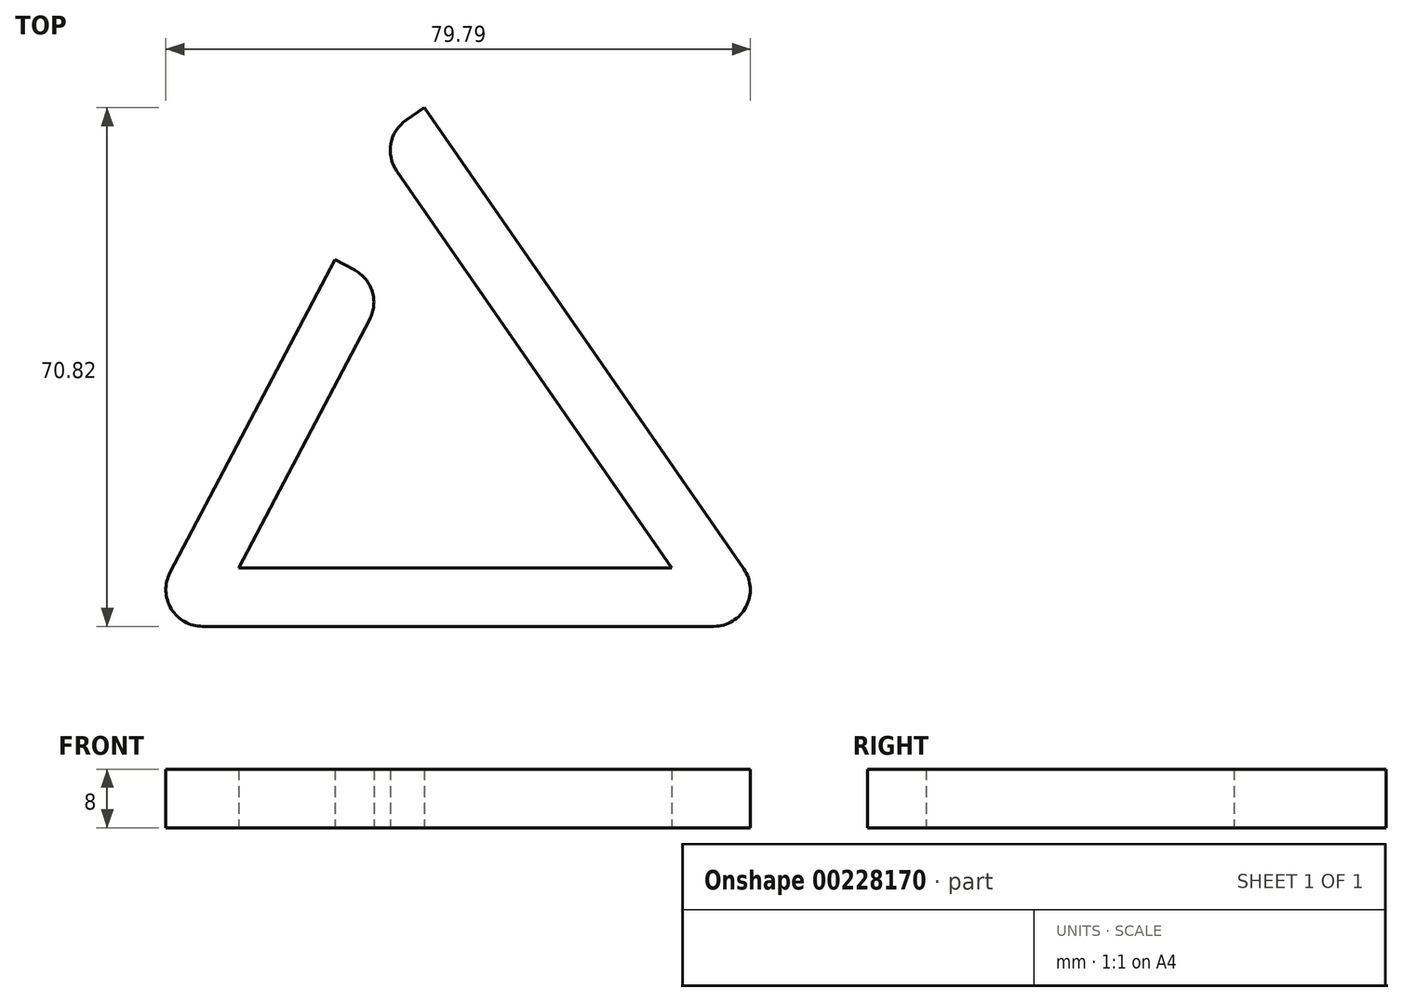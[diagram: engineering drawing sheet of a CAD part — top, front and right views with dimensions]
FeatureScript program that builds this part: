
annotation { "Feature Type Name" : "Feature", "Feature Type Description" : "" }
export const myFeature = defineFeature(function(context is Context, id is Id, definition is map)
    precondition{}
    {
        {
            var Q0;
            Q0=qCreatedBy(makeId("Top.planeOp"),FACE);
            var sketch = newSketch(context, id + "F0", { "sketchPlane" : qUnion([Q0])});
            skLineSegment(sketch, "E0", {"start": v(-30.26, -25.53) * mm, "end": v(39.53, -25.53) * mm});
            skLineSegment(sketch, "E1", {"start": v(43.64, -17.68) * mm, "end": v(0, 45.3) * mm});
            skLineSegment(sketch, "E2", {"start": v(-34.68, -18.2) * mm, "end": v(-12.19, 24.54) * mm});
            skLineSegment(sketch, "E3.0", {"start": v(-25.3, -17.53) * mm, "end": v(-7.44, 16.4) * mm});
            skLineSegment(sketch, "E3.1", {"start": v(-25.3, -17.53) * mm, "end": v(33.8, -17.53) * mm});
            skLineSegment(sketch, "E3.2", {"start": v(33.8, -17.53) * mm, "end": v(-3.73, 36.63) * mm});
            skLineSegment(sketch, "E4", {"start": v(-12.19, 24.54) * mm, "end": v(-9.53, 23.14) * mm});
            skLineSegment(sketch, "E5", {"start": v(-2.47, 43.59) * mm, "end": v(0, 45.3) * mm});
            skPoint(sketch, "E6.visualSharp", {"position": v(-38.54, -25.53) * mm});
            skArc(sketch, "E6.filletArc", {"start": v(-34.68, -18.2) * mm, "mid": v(-34.54, -23.11) * mm, "end": v(-30.26, -25.53) * mm});
            skPoint(sketch, "E7.visualSharp", {"position": v(49.08, -25.53) * mm});
            skArc(sketch, "E7.filletArc", {"start": v(39.53, -25.53) * mm, "mid": v(43.96, -22.85) * mm, "end": v(43.64, -17.68) * mm});
            skPoint(sketch, "E8.visualSharp", {"position": v(-6.58, 40.74) * mm});
            skArc(sketch, "E8.filletArc", {"start": v(-2.47, 43.59) * mm, "mid": v(-4.54, 40.37) * mm, "end": v(-3.73, 36.63) * mm});
            skPoint(sketch, "E9.visualSharp", {"position": v(-5.1, 20.82) * mm});
            skArc(sketch, "E9.filletArc", {"start": v(-7.44, 16.4) * mm, "mid": v(-7.09, 20.2) * mm, "end": v(-9.53, 23.14) * mm});
            skSolve(sketch);
        }
        {
            var Q0;
            Q0=makeQuery(id+"F0.imprint","IMPRINT",FACE,{"disambiguationData":[TD([[makeQuery(id+"F0.imprint","IMPRINT",EDGE,{"derivedFrom":sQuery(id+"F0.wireOp",EDGE,"E0")}),1.0]])]});
            extrude(context, id + "F1", {"entities" : qUnion([Q0]), "depth" : 8 * mm});
        }
    });
